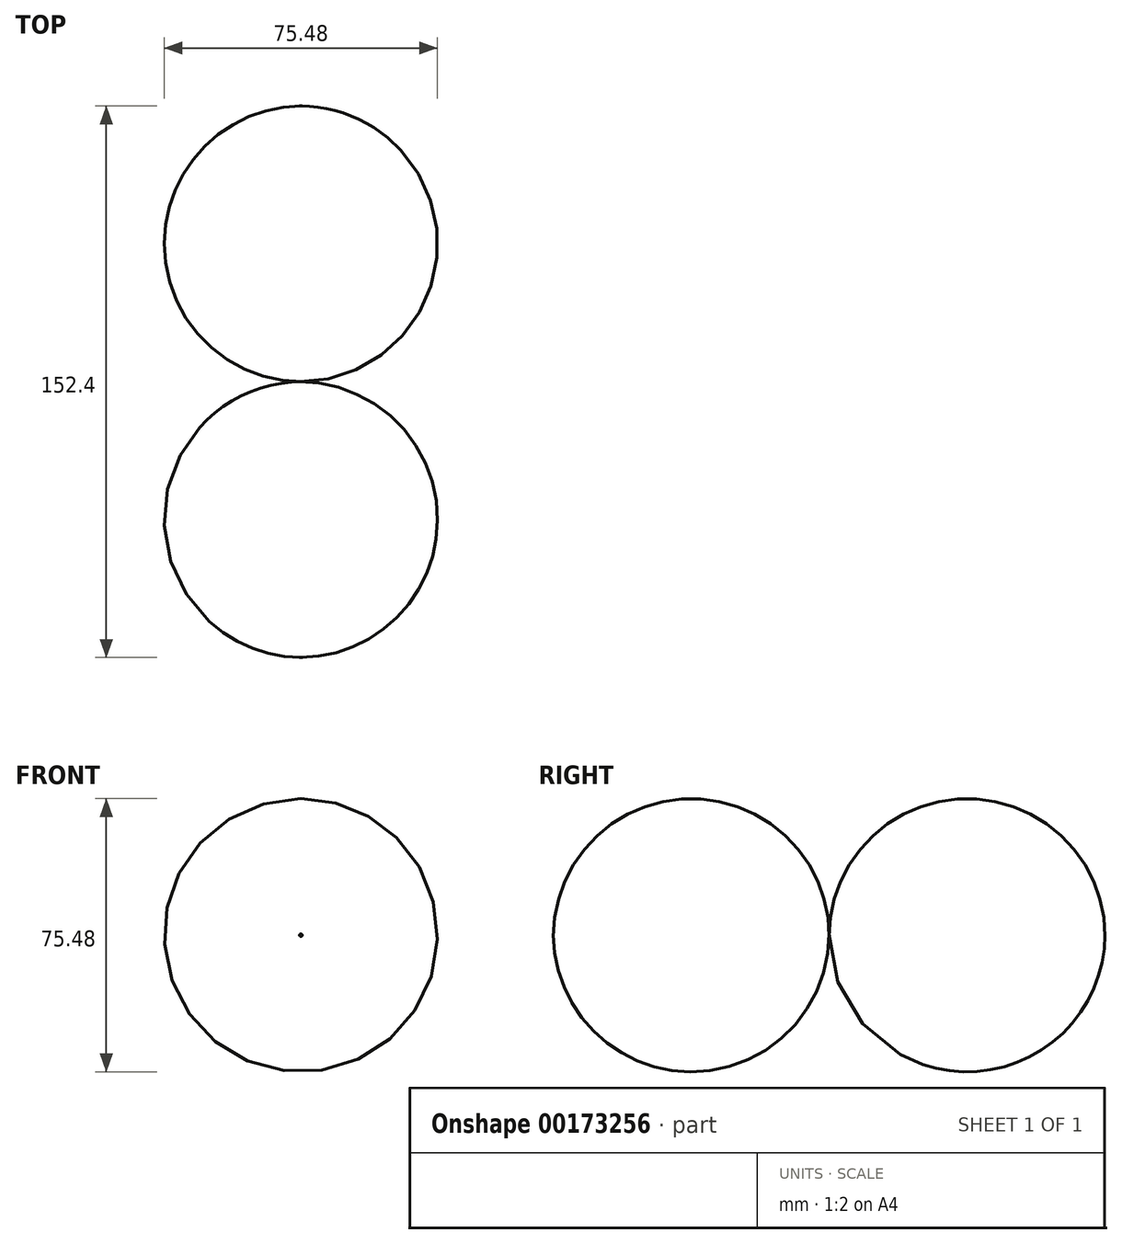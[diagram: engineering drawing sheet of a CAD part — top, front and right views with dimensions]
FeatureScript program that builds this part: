
annotation { "Feature Type Name" : "Feature", "Feature Type Description" : "" }
export const myFeature = defineFeature(function(context is Context, id is Id, definition is map)
    precondition{}
    {
        {
            var Q0;
            Q0=qCreatedBy(makeId("Front.planeOp"),FACE);
            var sketch = newSketch(context, id + "F0", { "sketchPlane" : qUnion([Q0])});
            skCircle(sketch, "E0", {"center": v(0, 0) * mm, "radius": 38.46 * mm});
            skLineSegment(sketch, "E1", {"start": v(0, 38.46) * mm, "end": v(0, -38.46) * mm});
            skSolve(sketch);
        }
        {
            var Q0;
            {var subQ0=sQuery(id+"F0.wireOp",EDGE,"E1");Q0=makeQuery(id+"F0.imprint","IMPRINT",FACE,{"disambiguationData":[TD([[makeQuery(id+"F0.imprint","IMPRINT",EDGE,{"derivedFrom":subQ0}),1.0]])]});}
            var Q1;
            {var subQ0=sQuery(id+"F0.wireOp",EDGE,"E1");Q1=makeQuery(id+"F0.imprint","IMPRINT",FACE,{"disambiguationData":[TD([[makeQuery(id+"F0.imprint","IMPRINT",EDGE,{"derivedFrom":subQ0}),-1.0]])]});}
            extrude(context, id + "F1", {"entities" : qUnion([Q0, Q1]), "depth" : 76.2 * mm});
        }
        {
            var Q0;
            Q0=makeQuery(id+"F1.opExtrude","SWEPT_FACE",FACE,{"disambiguationData":[OSD([sQuery(id+"F0.wireOp",EDGE,"E0")])]});
            var Q1;
            Q1=makeQuery(id+"F1.opExtrude","CAP_FACE",FACE,{"disambiguationData":[OSD([sQuery(id+"F0.wireOp",EDGE,"E0")])],"isStart":false});
            var Q2;
            Q2=makeQuery(id+"F1.opExtrude","CAP_EDGE",EDGE,{"disambiguationData":[OSD([sQuery(id+"F0.wireOp",EDGE,"E0")])],"isStart":true});
            fillet(context, id + "F2", {"entities" : qUnion([Q0, Q1, Q2]), "radius" : 38.1 * mm, "allowEdgeOverflow" : false});
        }
        {
            var Q0;
            Q0=makeQuery(id+"F1.opExtrude","SWEPT_BODY",BODY,{"disambiguationData":[OSD([sQuery(id+"F0.wireOp",EDGE,"E0")])]});
            var Q1;
            Q1=qCreatedBy(makeId("Front.planeOp"),FACE);
            mirror(context, id + "F3", {"operationType" : NewBodyOperationType.ADD, "entities" : qUnion([Q0]), "mirrorPlane" : qUnion([Q1])});
        }
    });
